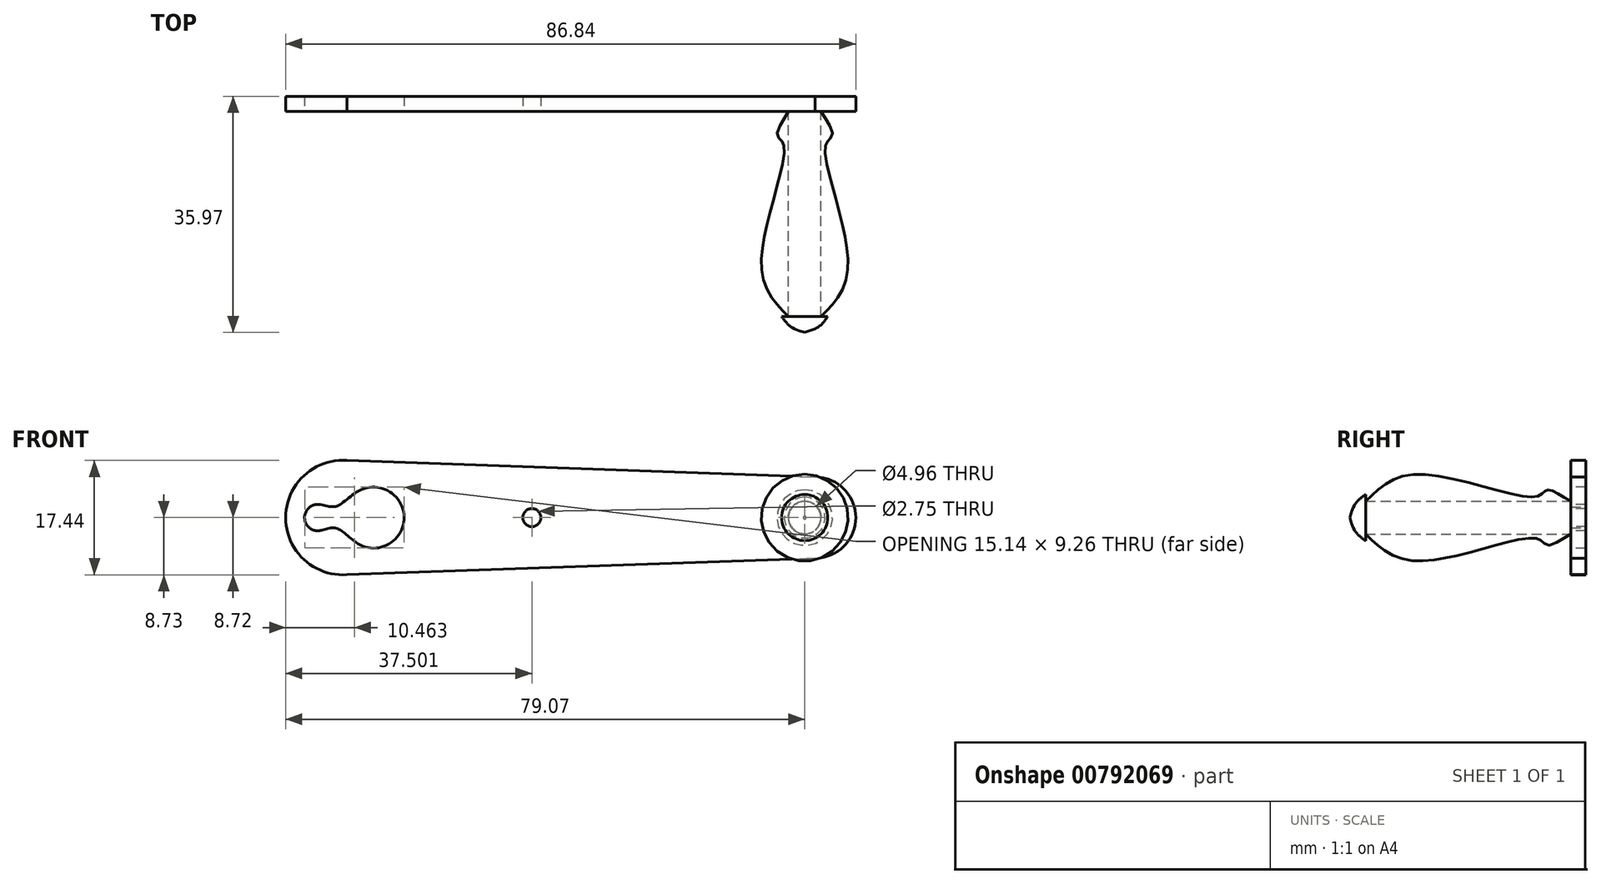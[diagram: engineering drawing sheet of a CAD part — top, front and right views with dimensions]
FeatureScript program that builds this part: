
annotation { "Feature Type Name" : "Feature", "Feature Type Description" : "" }
export const myFeature = defineFeature(function(context is Context, id is Id, definition is map)
    precondition{}
    {
        {
            var Q0;
            Q0=qCreatedBy(makeId("Front.planeOp"),FACE);
            var sketch = newSketch(context, id + "F0", { "sketchPlane" : qUnion([Q0])});
            skArc(sketch, "E0", {"start": v(-40.37, 8.7) * mm, "mid": v(-49.7, 0) * mm, "end": v(-40.37, -8.7) * mm});
            skArc(sketch, "E1", {"start": v(30.95, -6.18) * mm, "mid": v(37.13, 0) * mm, "end": v(30.95, 6.18) * mm});
            skLineSegment(sketch, "E2", {"start": v(-40.99, 8.72) * mm, "end": v(30.95, 6.18) * mm});
            skLineSegment(sketch, "E3", {"start": v(-40.99, -8.72) * mm, "end": v(30.95, -6.18) * mm});
            skSolve(sketch);
        }
        {
            var Q0;
            Q0=qSketchRegion(id+"F0",true);
            extrude(context, id + "F1", {"entities" : qUnion([Q0]), "depth" : 2.3 * mm, "offsetDistance" : 25 * mm});
        }
        {
            var Q0;
            Q0=makeQuery(id+"F1.opExtrude","CAP_FACE",FACE,{"disambiguationData":[OSD([sQuery(id+"F0.wireOp",EDGE,"E0"),sQuery(id+"F0.wireOp",EDGE,"E1"),sQuery(id+"F0.wireOp",EDGE,"E2"),sQuery(id+"F0.wireOp",EDGE,"E3")])],"isStart":false});
            var sketch = newSketch(context, id + "F2", { "sketchPlane" : qUnion([Q0])});
            skCircle(sketch, "E4", {"center": v(-44.83, 0) * mm, "radius": 2 * mm});
            skCircle(sketch, "E5", {"center": v(-36.31, 0) * mm, "radius": 4.64 * mm});
            skPoint(sketch, "E6", {"position": v(-46.83, 0) * mm});
            skPoint(sketch, "E7", {"position": v(-31.67, 0) * mm});
            skPoint(sketch, "E8", {"position": v(-12.2, 0) * mm});
            skCircle(sketch, "E9", {"center": v(-12.2, 0) * mm, "radius": 1.38 * mm});
            skCircle(sketch, "E10", {"center": v(29.35, 0) * mm, "radius": 2.5 * mm});
            skFitSpline(sketch, "E11", {"points": [v(-44.74, 2) * mm, v(-42.08, 1.7) * mm, v(-38.53, 4.08) * mm], "startDerivative": vector(7.35, -0.33) * mm, "endDerivative": vector(8.19, 4.45) * mm});
            skFitSpline(sketch, "E12", {"points": [v(-44.28, -1.92) * mm, v(-41.92, -1.64) * mm, v(-39.06, -3.75) * mm], "startDerivative": vector(5.48, 1.58) * mm, "endDerivative": vector(6.13, -4.49) * mm});
            skSolve(sketch);
        }
        {
            var Q0;
            {var subQ0=sQuery(id+"F2.wireOp",EDGE,"E5");var subQ1=makeQuery(id+"F2.imprint","INTERSECT",VERTEX,{"derivedFrom":[subQ0,sQuery(id+"F2.wireOp",EDGE,"JXqlM0UY-bxi7-qLzu-tcPN-rijKCx4FC96E")]});Q0=makeQuery(id+"F2.imprint","IMPRINT",FACE,{"disambiguationData":[TD([[makeQuery(id+"F2.imprint","IMPRINT",EDGE,{"disambiguationData":[TD([[subQ1,-1.0]])],"derivedFrom":subQ0}),1.0]])]});}
            var Q1;
            {var subQ0=sQuery(id+"F2.wireOp",EDGE,"E4");var subQ1=makeQuery(id+"F2.imprint","INTERSECT",VERTEX,{"derivedFrom":[subQ0,sQuery(id+"F2.wireOp",EDGE,"JXqlM0UY-bxi7-qLzu-tcPN-rijKCx4FC96E")]});Q1=makeQuery(id+"F2.imprint","IMPRINT",FACE,{"disambiguationData":[TD([[makeQuery(id+"F2.imprint","IMPRINT",EDGE,{"disambiguationData":[TD([[subQ1,-1.0]])],"derivedFrom":subQ0}),1.0]])]});}
            var Q2;
            {var subQ0=sQuery(id+"F2.wireOp",EDGE,"JXqlM0UY-bxi7-qLzu-tcPN-rijKCx4FC96E");Q2=makeQuery(id+"F2.imprint","IMPRINT",FACE,{"disambiguationData":[TD([[makeQuery(id+"F2.imprint","IMPRINT",EDGE,{"derivedFrom":subQ0}),-1.0]])]});}
            var Q3;
            Q3=makeQuery(id+"F2.imprint","IMPRINT",FACE,{"disambiguationData":[TD([[makeQuery(id+"F2.imprint","IMPRINT",EDGE,{"derivedFrom":sQuery(id+"F2.wireOp",EDGE,"E9")}),1.0]])]});
            var Q4;
            {var subQ0=sQuery(id+"F2.wireOp",EDGE,"E11");Q4=makeQuery(id+"F2.imprint","IMPRINT",FACE,{"disambiguationData":[TD([[makeQuery(id+"F2.imprint","IMPRINT",EDGE,{"derivedFrom":subQ0}),-1.0]])]});}
            extrude(context, id + "F3", {"entities" : qUnion([Q0, Q1, Q2, Q3, Q4]), "operationType" : NewBodyOperationType.REMOVE, "endBound" : BoundingType.UP_TO_NEXT, "oppositeDirection" : true, "depth" : 25 * mm, "offsetDistance" : 25 * mm});
        }
        {
            var Q0;
            Q0=makeQuery(id+"F2.imprint","IMPRINT",FACE,{"disambiguationData":[TD([[makeQuery(id+"F2.imprint","IMPRINT",EDGE,{"derivedFrom":sQuery(id+"F2.wireOp",EDGE,"E10")}),1.0]])]});
            extrude(context, id + "F4", {"entities" : qUnion([Q0]), "operationType" : NewBodyOperationType.ADD, "depth" : 31.27 * mm, "offsetDistance" : 25 * mm});
        }
        {
            var Q0;
            Q0=qCreatedBy(makeId("Top.planeOp"),FACE);
            var sketch = newSketch(context, id + "F5", { "sketchPlane" : qUnion([Q0])});
            skFitSpline(sketch, "E13", {"points": [v(31.84, -2.3) * mm, v(33.57, -5.94) * mm, v(32.54, -7.52) * mm, v(35.97, -25.41) * mm, v(31.84, -33.56) * mm], "startDerivative": vector(14.04, -23.1) * mm, "endDerivative": vector(-21.7, -21.75) * mm});
            skLineSegment(sketch, "E14.0", {"start": v(30.95, -2.3) * mm, "end": v(37.13, -2.3) * mm});
            skLineSegment(sketch, "E15", {"start": v(31.84, -2.3) * mm, "end": v(31.84, -33.56) * mm});
            skLineSegment(sketch, "E16", {"start": v(29.36, -2.32) * mm, "end": v(29.36, -33.41) * mm, "construction": true});
            skLineSegment(sketch, "E17", {"start": v(29.36, -35.97) * mm, "end": v(29.36, -33.41) * mm});
            skFitSpline(sketch, "E18", {"points": [v(29.36, -35.97) * mm, v(31.47, -35.12) * mm, v(32.88, -33.56) * mm], "startDerivative": vector(4.46, 1.28) * mm, "endDerivative": vector(2.56, 3.56) * mm});
            skLineSegment(sketch, "E19", {"start": v(31.84, -33.56) * mm, "end": v(32.88, -33.56) * mm});
            skLineSegment(sketch, "E20", {"start": v(29.36, -33.57) * mm, "end": v(32.88, -33.56) * mm});
            skSolve(sketch);
        }
        {
            var Q0;
            Q0=makeQuery(id+"F5.imprint","IMPRINT",FACE,{"disambiguationData":[TD([[makeQuery(id+"F5.imprint","IMPRINT",EDGE,{"derivedFrom":sQuery(id+"F5.wireOp",EDGE,"E13")}),-1.0]])]});
            var Q1;
            Q1=sQuery(id+"F5.wireOp",EDGE,"E13");
            var Q2;
            Q2=sQuery(id+"F5.wireOp",EDGE,"E16");
            revolve(context, id + "F6", {"entities" : qUnion([Q0]), "surfaceEntities" : qUnion([Q1]), "axis" : qUnion([Q2]), "revolveType" : RevolveType.FULL});
        }
        {
            var Q0;
            {var subQ0=sQuery(id+"F5.wireOp",EDGE,"E18");Q0=makeQuery(id+"F5.imprint","IMPRINT",FACE,{"disambiguationData":[TD([[makeQuery(id+"F5.imprint","IMPRINT",EDGE,{"derivedFrom":subQ0}),1.0]])]});}
            var Q1;
            Q1=sQuery(id+"F5.wireOp",EDGE,"E16");
            revolve(context, id + "F7", {"operationType" : NewBodyOperationType.ADD, "entities" : qUnion([Q0]), "axis" : qUnion([Q1]), "revolveType" : RevolveType.FULL});
        }
    });
